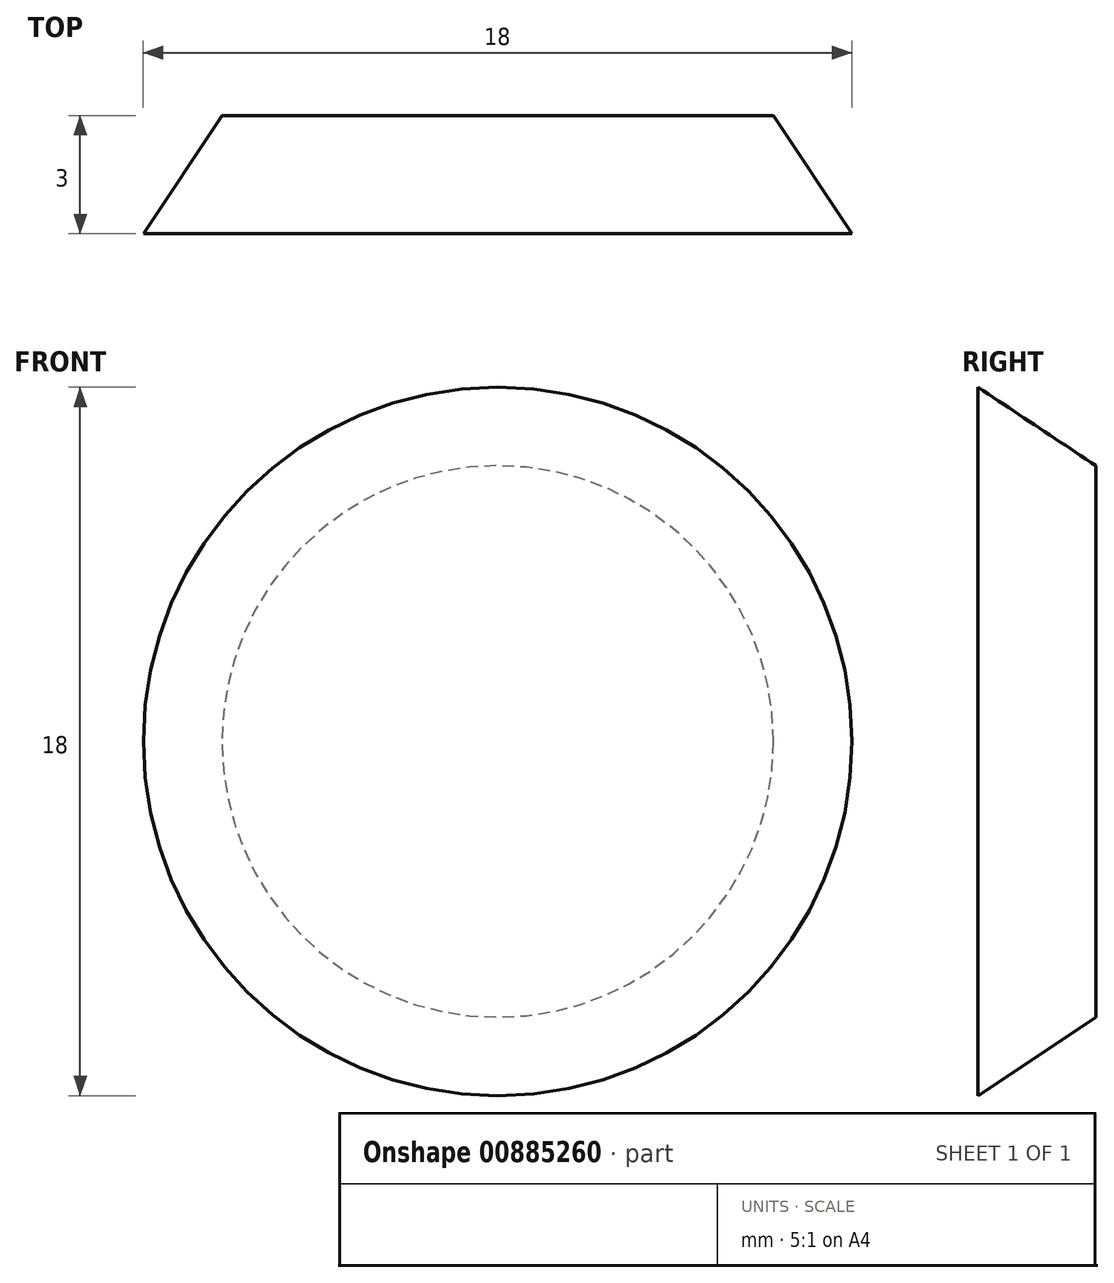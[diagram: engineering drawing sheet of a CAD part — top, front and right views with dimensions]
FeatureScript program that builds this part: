
annotation { "Feature Type Name" : "Feature", "Feature Type Description" : "" }
export const myFeature = defineFeature(function(context is Context, id is Id, definition is map)
    precondition{}
    {
        {
            var Q0;
            Q0=qCreatedBy(makeId("Top.planeOp"),FACE);
            var sketch = newSketch(context, id + "F0", { "sketchPlane" : qUnion([Q0])});
            skLineSegment(sketch, "E0", {"start": v(-54.84, -33.79) * mm, "end": v(-36.84, -33.79) * mm});
            skPoint(sketch, "E1", {"position": v(-45.84, -33.79) * mm});
            skLineSegment(sketch, "E2", {"start": v(-45.84, -33.79) * mm, "end": v(-45.84, -30.79) * mm});
            skLineSegment(sketch, "E3", {"start": v(-45.84, -30.79) * mm, "end": v(-52.84, -30.79) * mm});
            skLineSegment(sketch, "E4", {"start": v(-45.84, -30.79) * mm, "end": v(-38.83, -30.79) * mm});
            skLineSegment(sketch, "E5", {"start": v(-52.84, -30.79) * mm, "end": v(-54.84, -33.79) * mm});
            skLineSegment(sketch, "E6", {"start": v(-38.83, -30.79) * mm, "end": v(-36.84, -33.79) * mm});
            skPoint(sketch, "E7", {"position": v(-54.32, -33.01) * mm});
            skPoint(sketch, "E8", {"position": v(-37.49, -32.8) * mm});
            skLineSegment(sketch, "E9", {"start": v(-38.83, -30.79) * mm, "end": v(-38.83, -33.79) * mm});
            skLineSegment(sketch, "E10", {"start": v(-52.84, -30.79) * mm, "end": v(-52.84, -33.79) * mm});
            skLineSegment(sketch, "E11", {"start": v(-45.84, -30.2) * mm, "end": v(-45.84, -37.89) * mm});
            skPoint(sketch, "E12.third.point", {"position": v(-44.53, -34.68) * mm});
            skLineSegment(sketch, "E13", {"start": v(-45.84, -28.67) * mm, "end": v(-45.84, -37.89) * mm});
            skSolve(sketch);
        }
        {
            var Q0;
            {var subQ0=sQuery(id+"F0.wireOp",EDGE,"E5");Q0=makeQuery(id+"F0.imprint","IMPRINT",FACE,{"disambiguationData":[TD([[makeQuery(id+"F0.imprint","IMPRINT",EDGE,{"derivedFrom":subQ0}),1.0]])]});}
            var Q1;
            {var subQ4=sQuery(id+"F0.wireOp",EDGE,"E3");Q1=makeQuery(id+"F0.imprint","IMPRINT",FACE,{"disambiguationData":[TD([[makeQuery(id+"F0.imprint","IMPRINT",EDGE,{"derivedFrom":subQ4}),1.0]])]});}
            var Q2;
            {var subQ1=sQuery(id+"F0.wireOp",EDGE,"E0");var subQ3=makeQuery(id+"F0.imprint","INTERSECT",VERTEX,{"derivedFrom":[subQ1,sQuery(id+"F0.wireOp",EDGE,"E10")]});Q2=makeQuery(id+"F0.imprint","IMPRINT",FACE,{"disambiguationData":[TD([[makeQuery(id+"F0.imprint","IMPRINT",EDGE,{"disambiguationData":[TD([[subQ3,-1.0]])],"derivedFrom":subQ1}),-1.0]])]});}
            var Q3;
            Q3=sQuery(id+"F0.wireOp",EDGE,"E13");
            revolve(context, id + "F1", {"surfaceOperationType" : NewSurfaceOperationType.NEW, "entities" : qUnion([Q0, Q1, Q2]), "axis" : qUnion([Q3]), "revolveType" : RevolveType.FULL});
        }
    });
